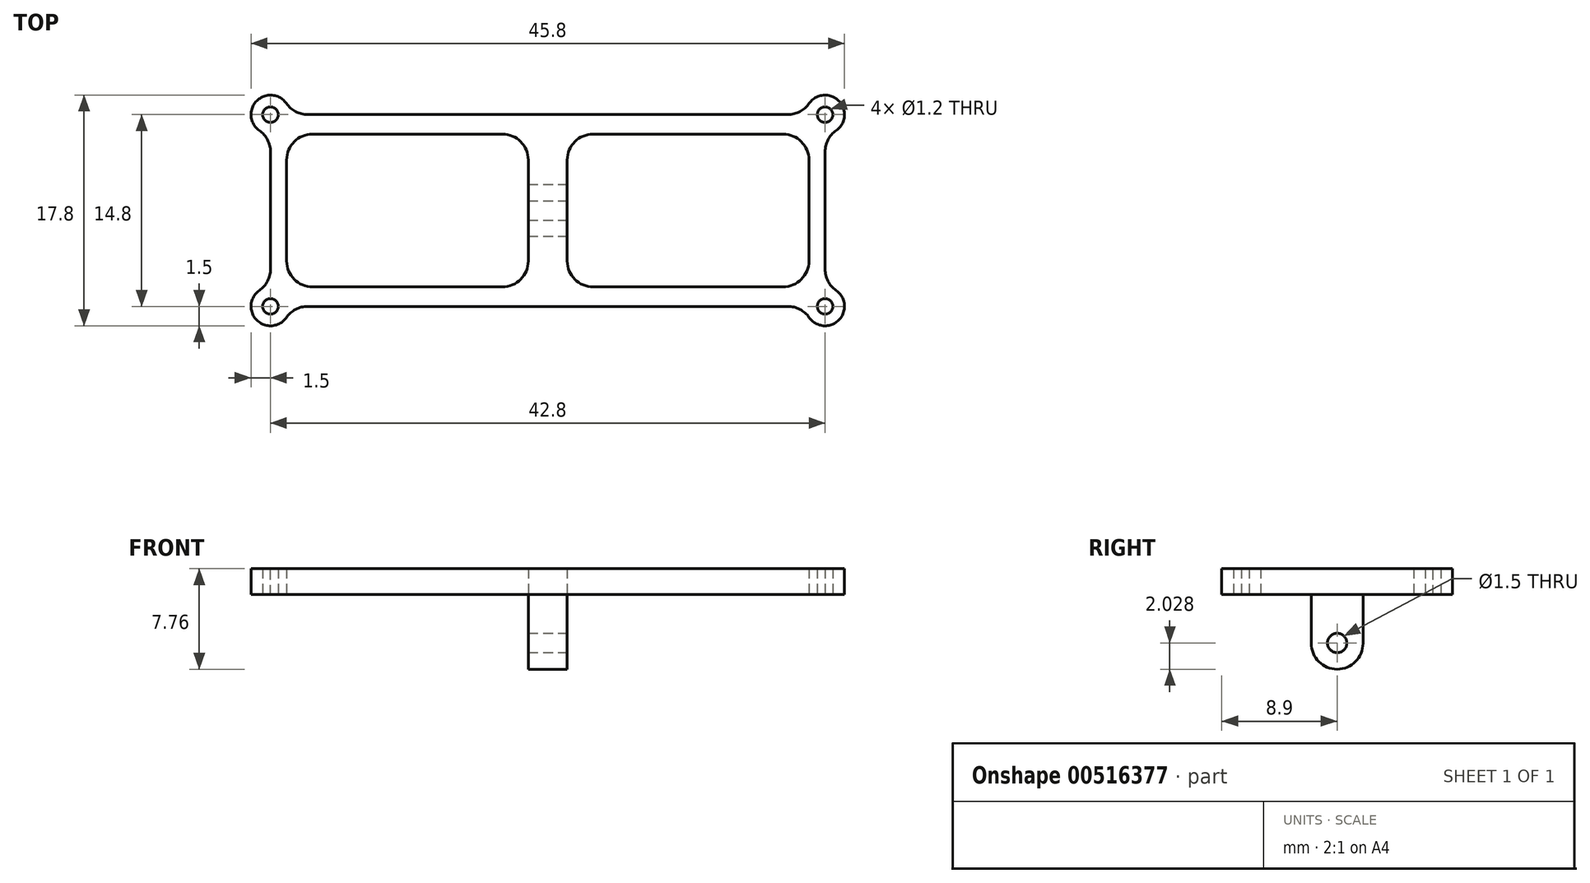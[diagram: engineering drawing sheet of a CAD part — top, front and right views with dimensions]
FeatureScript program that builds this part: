
annotation { "Feature Type Name" : "Feature", "Feature Type Description" : "" }
export const myFeature = defineFeature(function(context is Context, id is Id, definition is map)
    precondition{}
    {
        {
            var Q0;
            Q0=qCreatedBy(makeId("Top.planeOp"),FACE);
            var sketch = newSketch(context, id + "F0", { "sketchPlane" : qUnion([Q0])});
            skLineSegment(sketch, "E0.bottom", {"start": v(21.4, 7.4) * mm, "end": v(-21.4, 7.4) * mm});
            skLineSegment(sketch, "E0.top", {"start": v(21.4, -7.4) * mm, "end": v(-21.4, -7.4) * mm});
            skLineSegment(sketch, "E0.left", {"start": v(21.4, 7.4) * mm, "end": v(21.4, -7.4) * mm});
            skLineSegment(sketch, "E0.right", {"start": v(-21.4, 7.4) * mm, "end": v(-21.4, -7.4) * mm});
            skPoint(sketch, "E0.middle", {"position": v(0, 0) * mm});
            skCircle(sketch, "E1", {"center": v(-21.4, 7.4) * mm, "radius": 0.6 * mm});
            skCircle(sketch, "E2", {"center": v(-21.4, -7.4) * mm, "radius": 0.6 * mm});
            skCircle(sketch, "E3", {"center": v(21.4, -7.4) * mm, "radius": 0.6 * mm});
            skCircle(sketch, "E4", {"center": v(21.4, 7.4) * mm, "radius": 0.6 * mm});
            skCircle(sketch, "E5", {"center": v(-21.4, 7.4) * mm, "radius": 1.5 * mm});
            skCircle(sketch, "E6", {"center": v(-21.4, -7.4) * mm, "radius": 1.5 * mm});
            skCircle(sketch, "E7", {"center": v(21.4, -7.4) * mm, "radius": 1.5 * mm});
            skCircle(sketch, "E8", {"center": v(21.4, 7.4) * mm, "radius": 1.5 * mm});
            skLineSegment(sketch, "E9.right", {"start": v(20.43, 6.6) * mm, "end": v(20.43, -6.6) * mm});
            skLineSegment(sketch, "E10.bottom", {"start": v(-1.5, 6.6) * mm, "end": v(1.5, 6.6) * mm});
            skLineSegment(sketch, "E10.top", {"start": v(-1.5, -6.6) * mm, "end": v(1.5, -6.6) * mm});
            skLineSegment(sketch, "E10.left", {"start": v(-1.5, 6.6) * mm, "end": v(-1.5, -6.6) * mm});
            skLineSegment(sketch, "E10.right", {"start": v(1.5, 6.6) * mm, "end": v(1.5, -6.6) * mm});
            skLineSegment(sketch, "E11.bottom", {"start": v(-20.16, -5.9) * mm, "end": v(20.16, -5.9) * mm});
            skLineSegment(sketch, "E11.top", {"start": v(-20.16, 5.9) * mm, "end": v(20.16, 5.9) * mm});
            skLineSegment(sketch, "E11.left", {"start": v(-20.16, -5.9) * mm, "end": v(-20.16, 5.9) * mm});
            skLineSegment(sketch, "E11.right", {"start": v(20.16, -5.9) * mm, "end": v(20.16, 5.9) * mm});
            skSolve(sketch);
        }
        {
            var Q0;
            Q0 = qSketchRegion(id + "F0", true);
            var Q1;
            Q1=makeQuery(id+"F0.imprint","IMPRINT",FACE,{"disambiguationData":[TD([[makeQuery(id+"F0.imprint","IMPRINT",EDGE,{"derivedFrom":sQuery(id+"F0.wireOp",EDGE,"E10.bottom")}),-1.0]])]});
            var Q2;
            {var subQ0=sQuery(id+"F0.wireOp",EDGE,"E10.top");Q2=makeQuery(id+"F0.imprint","IMPRINT",FACE,{"disambiguationData":[TD([[makeQuery(id+"F0.imprint","IMPRINT",EDGE,{"derivedFrom":subQ0}),1.0]])]});}
            var Q3;
            {var subQ0=sQuery(id+"F0.wireOp",EDGE,"E11.top");var subQ1=sQuery(id+"F0.wireOp",EDGE,"E10.left");var subQ2=makeQuery(id+"F0.imprint","INTERSECT",VERTEX,{"derivedFrom":[subQ1,subQ0]});Q3=makeQuery(id+"F0.imprint","IMPRINT",FACE,{"disambiguationData":[TD([[makeQuery(id+"F0.imprint","IMPRINT",EDGE,{"disambiguationData":[TD([[subQ2,-1.0]])],"derivedFrom":subQ1}),1.0]])]});}
            extrude(context, id + "F1", {"entities" : qUnion([Q0, Q1, Q2, Q3]), "depth" : 2 * mm, "offsetDistance" : 25 * mm});
        }
        {
            var Q0;
            Q0=makeQuery(id+"F1.opExtrude","SWEPT_EDGE",EDGE,{"disambiguationData":[OSD([sQuery(id+"F0.wireOp",EDGE,"E5"),sQuery(id+"F0.wireOp",EDGE,"E9.bottom"),sQuery(id+"F0.wireOp",EDGE,"E9.left")])]});
            var Q1;
            Q1=makeQuery(id+"F1.opExtrude","SWEPT_EDGE",EDGE,{"disambiguationData":[OSD([sQuery(id+"F0.wireOp",EDGE,"E6"),sQuery(id+"F0.wireOp",EDGE,"E9.top"),sQuery(id+"F0.wireOp",EDGE,"E9.left")])]});
            var Q2;
            Q2=makeQuery(id+"F1.opExtrude","SWEPT_EDGE",EDGE,{"disambiguationData":[OSD([sQuery(id+"F0.wireOp",EDGE,"E8"),sQuery(id+"F0.wireOp",EDGE,"E9.bottom"),sQuery(id+"F0.wireOp",EDGE,"E9.right")])]});
            var Q3;
            Q3=makeQuery(id+"F1.opExtrude","SWEPT_EDGE",EDGE,{"disambiguationData":[OSD([sQuery(id+"F0.wireOp",EDGE,"E7"),sQuery(id+"F0.wireOp",EDGE,"E9.top"),sQuery(id+"F0.wireOp",EDGE,"E9.right")])]});
            var Q4;
            Q4=makeQuery(id+"F1.opExtrude","SWEPT_EDGE",EDGE,{"disambiguationData":[OSD([sQuery(id+"F0.wireOp",EDGE,"E10.left"),sQuery(id+"F0.wireOp",EDGE,"E11.bottom")])]});
            var Q5;
            Q5=makeQuery(id+"F1.opExtrude","SWEPT_EDGE",EDGE,{"disambiguationData":[OSD([sQuery(id+"F0.wireOp",EDGE,"E11.bottom"),sQuery(id+"F0.wireOp",EDGE,"E11.left")])]});
            var Q6;
            Q6=makeQuery(id+"F1.opExtrude","SWEPT_EDGE",EDGE,{"disambiguationData":[OSD([sQuery(id+"F0.wireOp",EDGE,"E11.top"),sQuery(id+"F0.wireOp",EDGE,"E11.left")])]});
            var Q7;
            Q7=makeQuery(id+"F1.opExtrude","SWEPT_EDGE",EDGE,{"disambiguationData":[OSD([sQuery(id+"F0.wireOp",EDGE,"E11.top"),sQuery(id+"F0.wireOp",EDGE,"E11.right")])]});
            var Q8;
            Q8=makeQuery(id+"F1.opExtrude","SWEPT_EDGE",EDGE,{"disambiguationData":[OSD([sQuery(id+"F0.wireOp",EDGE,"E11.bottom"),sQuery(id+"F0.wireOp",EDGE,"E11.right")])]});
            var Q9;
            Q9=makeQuery(id+"F1.opExtrude","SWEPT_EDGE",EDGE,{"disambiguationData":[OSD([sQuery(id+"F0.wireOp",EDGE,"E10.right"),sQuery(id+"F0.wireOp",EDGE,"E11.top")])]});
            var Q10;
            Q10=makeQuery(id+"F1.opExtrude","SWEPT_EDGE",EDGE,{"disambiguationData":[OSD([sQuery(id+"F0.wireOp",EDGE,"E10.left"),sQuery(id+"F0.wireOp",EDGE,"E11.top")])]});
            var Q11;
            Q11=makeQuery(id+"F1.opExtrude","SWEPT_EDGE",EDGE,{"disambiguationData":[OSD([sQuery(id+"F0.wireOp",EDGE,"E10.right"),sQuery(id+"F0.wireOp",EDGE,"E11.bottom")])]});
            fillet(context, id + "F2", {"entities" : qUnion([Q0, Q1, Q2, Q3, Q4, Q5, Q6, Q7, Q8, Q9, Q10, Q11]), "radius" : 2 * mm, "tangentPropagation" : true, "allowEdgeOverflow" : false});
        }
        {
            var Q0;
            Q0=makeQuery(id+"F1.opExtrude","SWEPT_FACE",FACE,{"disambiguationData":[OSD([sQuery(id+"F0.wireOp",EDGE,"E10.right")])]});
            var sketch = newSketch(context, id + "F3", { "sketchPlane" : qUnion([Q0])});
            skLineSegment(sketch, "E12.bottom", {"start": v(2, 2) * mm, "end": v(-2, 2) * mm});
            skLineSegment(sketch, "E12.top", {"start": v(2, -5.76) * mm, "end": v(-2, -5.76) * mm});
            skLineSegment(sketch, "E12.left", {"start": v(2, 2) * mm, "end": v(2, -5.76) * mm});
            skLineSegment(sketch, "E12.right", {"start": v(-2, 2) * mm, "end": v(-2, -5.76) * mm});
            skCircle(sketch, "E13", {"center": v(0, -3.73) * mm, "radius": 0.75 * mm});
            skLineSegment(sketch, "E14", {"start": v(0, 0) * mm, "end": v(0, 2) * mm, "construction": true});
            skSolve(sketch);
        }
        {
            var Q0;
            Q0 = qSketchRegion(id + "F3", true);
            var Q1;
            Q1=makeQuery(id+"F1.opExtrude","SWEPT_FACE",FACE,{"disambiguationData":[OSD([sQuery(id+"F0.wireOp",EDGE,"E10.left")])]});
            extrude(context, id + "F4", {"entities" : qUnion([Q0]), "operationType" : NewBodyOperationType.ADD, "endBound" : BoundingType.UP_TO_SURFACE, "oppositeDirection" : true, "depth" : 25 * mm, "endBoundEntityFace" : qUnion([Q1]), "offsetDistance" : 25 * mm});
        }
        {
            var Q0;
            Q0=makeQuery(id+"F4.opExtrude","SWEPT_EDGE",EDGE,{"disambiguationData":[OSD([sQuery(id+"F3.wireOp",EDGE,"E12.top"),sQuery(id+"F3.wireOp",EDGE,"E12.left")])]});
            var Q1;
            Q1=makeQuery(id+"F4.opExtrude","SWEPT_EDGE",EDGE,{"disambiguationData":[OSD([sQuery(id+"F3.wireOp",EDGE,"E12.top"),sQuery(id+"F3.wireOp",EDGE,"E12.right")])]});
            fillet(context, id + "F5", {"entities" : qUnion([Q0, Q1]), "radius" : 2 * mm, "tangentPropagation" : true, "allowEdgeOverflow" : false});
        }
    });
